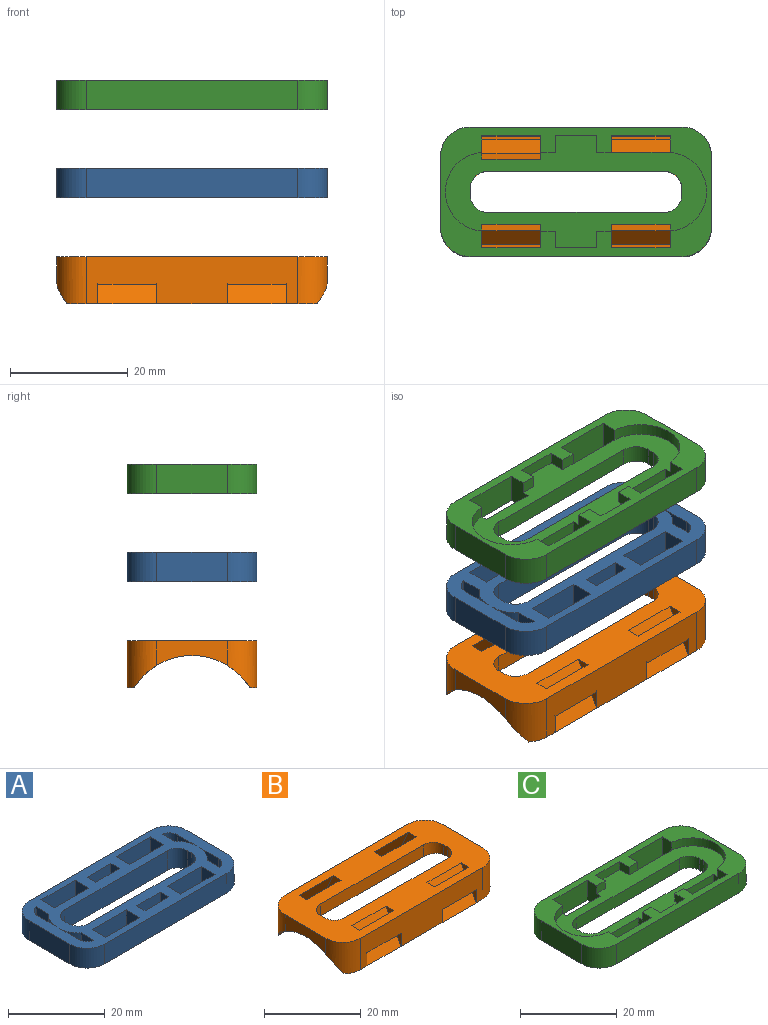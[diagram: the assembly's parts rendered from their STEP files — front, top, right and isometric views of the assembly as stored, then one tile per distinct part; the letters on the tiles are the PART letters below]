
ASSEMBLY  parts=3 mates=2
PART A: 58 faces, bbox 46x22x5 mm
  f0: plane 46x22mm, normal (0,0,1), area 516.2mm2, adj f2,f3,f4,f5,f6,f7,f8,f9
  f1: plane 46x22mm, normal (0,0,-1), area 516.2mm2, adj f2,f3,f4,f5,f6,f7,f8,f9
  f2: plane 36x5mm, normal (0,-1,0), area 180mm2, adj f0,f1,f26,f29
  f3: plane 12x5mm, normal (1,0,0), area 60mm2, adj f0,f1,f26,f27
  f4: plane 36x5mm, normal (0,1,0), area 180mm2, adj f0,f1,f27,f28
  f5: plane 5x1mm, normal (-1,0,0), area 5mm2, adj f0,f1,f30,f33
  f6: plane 30x5mm, normal (0,1,0), area 150mm2, adj f0,f1,f30,f31
  f7: plane 5x1mm, normal (1,0,0), area 5mm2, adj f0,f1,f31,f32
  f8: plane 30x5mm, normal (0,-1,0), area 150mm2, adj f0,f1,f32,f33
  f9: plane 12x5mm, normal (-1,0,0), area 60mm2, adj f0,f1,f28,f29
  f10: plane 10x5mm, normal (0,-1,0), area 50mm2, adj f0,f1,f11,f13
  f11: plane 5x4mm, normal (1,0,0), area 20mm2, adj f0,f1,f10,f12
  f12: plane 10x5mm, normal (0,1,0), area 50mm2, adj f0,f1,f11,f13
  f13: plane 5x4mm, normal (-1,0,0), area 20mm2, adj f0,f1,f10,f12
  f14: plane 10x5mm, normal (0,1,0), area 50mm2, adj f0,f1,f15,f17
  f15: plane 5x4mm, normal (-1,0,0), area 20mm2, adj f0,f1,f14,f16
  f16: plane 10x5mm, normal (0,-1,0), area 50mm2, adj f0,f1,f15,f17
  f17: plane 5x4mm, normal (1,0,0), area 20mm2, adj f0,f1,f14,f16
  f18: plane 5x4mm, normal (-1,0,0), area 20mm2, adj f0,f1,f19,f21
  f19: plane 10x5mm, normal (0,-1,0), area 50mm2, adj f0,f1,f18,f20
  f20: plane 5x4mm, normal (1,0,0), area 20mm2, adj f0,f1,f19,f21
  f21: plane 10x5mm, normal (0,1,0), area 50mm2, adj f0,f1,f18,f20
  f22: plane 5x4mm, normal (-1,0,0), area 20mm2, adj f0,f1,f23,f25
  f23: plane 10x5mm, normal (0,-1,0), area 50mm2, adj f0,f1,f22,f24
  f24: plane 5x4mm, normal (1,0,0), area 20mm2, adj f0,f1,f23,f25
  f25: plane 10x5mm, normal (0,1,0), area 50mm2, adj f0,f1,f22,f24
  f26: cylinder r=5mm len=5mm, axis (0,0,1), area 39.3mm2, adj f0,f1,f2,f3
  f27: cylinder r=5mm len=5mm, axis (0,0,-1), area 39.3mm2, adj f0,f1,f3,f4
  f28: cylinder r=5mm len=5mm, axis (0,0,1), area 39.3mm2, adj f0,f1,f4,f9
  f29: cylinder r=5mm len=5mm, axis (0,0,-1), area 39.3mm2, adj f0,f1,f2,f9
  f30: cylinder r=3mm len=5mm, axis (0,0,-1), area 23.6mm2, adj f0,f1,f5,f6
  f31: cylinder r=3mm len=5mm, axis (0,0,1), area 23.6mm2, adj f0,f1,f6,f7
  f32: cylinder r=3mm len=5mm, axis (0,0,-1), area 23.6mm2, adj f0,f1,f7,f8
  f33: cylinder r=3mm len=5mm, axis (0,0,1), area 23.6mm2, adj f0,f1,f5,f8
  f34: plane 5x2.5mm, normal (1,0,0), area 12.5mm2, adj f0,f1,f36,f37
  f35: plane 5x2.5mm, normal (-1,0,0), area 12.5mm2, adj f0,f1,f36,f37
  f36: plane 7x5mm, normal (0,-1,0), area 35mm2, adj f0,f1,f34,f35
  f37: plane 7x5mm, normal (0,1,0), area 35mm2, adj f0,f1,f34,f35
  f38: cylinder r=5.5mm len=5mm, axis (0,0,-1), area 24.2mm2, adj f0,f1,f40,f41
  f39: cylinder r=2.5mm len=5mm, axis (0,0,1), area 17.1mm2, adj f0,f1,f40,f41
  f40: plane 5x3.71mm, normal (1,0,0), area 18.5mm2, adj f0,f1,f38,f39
  f41: plane 5.5x5mm, normal (-1,0,0), area 27.5mm2, adj f0,f1,f38,f39
  f42: cylinder r=5.5mm len=5mm, axis (0,0,1), area 24.2mm2, adj f0,f1,f44,f45
  f43: cylinder r=2.5mm len=5mm, axis (0,0,-1), area 17.1mm2, adj f0,f1,f44,f45
  f44: plane 5x3.71mm, normal (-1,0,0), area 18.5mm2, adj f0,f1,f42,f43
  f45: plane 5.5x5mm, normal (1,0,0), area 27.5mm2, adj f0,f1,f42,f43
  f46: cylinder r=5.5mm len=5mm, axis (0,0,1), area 24.2mm2, adj f0,f1,f48,f49
  f47: cylinder r=2.5mm len=5mm, axis (0,0,-1), area 17.1mm2, adj f0,f1,f48,f49
  f48: plane 5x3.71mm, normal (1,0,0), area 18.5mm2, adj f0,f1,f46,f47
  f49: plane 5.5x5mm, normal (-1,0,0), area 27.5mm2, adj f0,f1,f46,f47
  f50: plane 7x5mm, normal (0,-1,0), area 35mm2, adj f0,f1,f52,f53
  f51: plane 7x5mm, normal (0,1,0), area 35mm2, adj f0,f1,f52,f53
  f52: plane 5x2.5mm, normal (1,0,0), area 12.5mm2, adj f0,f1,f50,f51
  f53: plane 5x2.5mm, normal (-1,0,0), area 12.5mm2, adj f0,f1,f50,f51
  f54: cylinder r=5.5mm len=5mm, axis (0,0,-1), area 24.2mm2, adj f0,f1,f56,f57
  f55: cylinder r=2.5mm len=5mm, axis (0,0,1), area 17.1mm2, adj f0,f1,f56,f57
  f56: plane 5x3.71mm, normal (-1,0,0), area 18.5mm2, adj f0,f1,f54,f55
  f57: plane 5.5x5mm, normal (1,0,0), area 27.5mm2, adj f0,f1,f54,f55
PART B: 36 faces, bbox 46x22x8 mm
  f0: plane 42.47x1.19mm, normal (0,0,-1), area 48.1mm2, adj f4,f13,f14,f15,f23,f27
  f1: plane 12x4.19mm, normal (1,0,0), area 36.5mm2, adj f10,f11,f14,f15
  f2: plane 36x8mm, normal (0,1,0), area 221.3mm2, adj f9,f10,f11,f12,f28,f29,f30,f32
  f3: plane 12x4.19mm, normal (-1,0,0), area 36.5mm2, adj f10,f12,f13,f15
  f4: plane 36x8mm, normal (0,-1,0), area 221.3mm2, adj f0,f10,f13,f14,f20,f21,f22,f24
  f5: plane 2.51x1mm, normal (-1,0,0), area 2.5mm2, adj f10,f15,f16,f19
  f6: plane 30x3.05mm, normal (0,1,0), area 91.4mm2, adj f10,f15,f16,f17
  f7: plane 2.51x1mm, normal (1,0,0), area 2.5mm2, adj f10,f15,f17,f18
  f8: plane 30x3.05mm, normal (0,-1,0), area 91.4mm2, adj f10,f15,f18,f19
  f9: plane 42.47x1.19mm, normal (0,0,-1), area 48.1mm2, adj f2,f11,f12,f15,f31,f35
  f10: plane 46x22mm, normal (0,0,1), area 654.3mm2, adj f1,f2,f3,f4,f5,f6,f7,f8
  f11: cylinder r=5mm len=8mm, axis (0,0,-1), area 53.8mm2, adj f1,f2,f9,f10,f15
  f12: cylinder r=5mm len=8mm, axis (0,0,1), area 53.8mm2, adj f2,f3,f9,f10,f15
  f13: cylinder r=5mm len=8mm, axis (0,0,-1), area 53.8mm2, adj f0,f3,f4,f10,f15
  f14: cylinder r=5mm len=8mm, axis (0,0,1), area 53.8mm2, adj f0,f1,f4,f10,f15
  f15: cylinder r=11.5mm len=46mm, axis (-1,0,0), area 819.8mm2, adj f0,f1,f3,f5,f6,f7,f8,f9
  f16: cylinder r=3mm len=3.05mm, axis (0,0,-1), area 13.2mm2, adj f5,f6,f10,f15
  f17: cylinder r=3mm len=3.05mm, axis (0,0,1), area 13.2mm2, adj f6,f7,f10,f15
  f18: cylinder r=3mm len=3.05mm, axis (0,0,-1), area 13.2mm2, adj f7,f8,f10,f15
  f19: cylinder r=3mm len=3.05mm, axis (0,0,1), area 13.2mm2, adj f5,f8,f10,f15
  f20: plane 8x4.4mm, normal (1,0,0), area 12.7mm2, adj f4,f10,f21,f23
  f21: plane 10x4.67mm, normal (0,0.91,-0.41), area 51.2mm2, adj f4,f10,f20,f22
  f22: plane 8x4.4mm, normal (-1,0,0), area 12.7mm2, adj f4,f10,f21,f23
  f23: plane 10x8mm, normal (0,-0.88,0.48), area 91.3mm2, adj f0,f10,f20,f22
  f24: plane 8x4.4mm, normal (-1,0,0), area 12.7mm2, adj f4,f10,f25,f27
  f25: plane 10x4.67mm, normal (0,0.91,-0.41), area 51.2mm2, adj f4,f10,f24,f26
  f26: plane 8x4.4mm, normal (1,0,0), area 12.7mm2, adj f4,f10,f25,f27
  f27: plane 10x8mm, normal (0,-0.88,0.48), area 91.3mm2, adj f0,f10,f24,f26
  f28: plane 8x4.4mm, normal (-1,0,0), area 12.7mm2, adj f2,f10,f29,f31
  f29: plane 10x4.67mm, normal (0,-0.91,-0.41), area 51.2mm2, adj f2,f10,f28,f30
  f30: plane 8x4.4mm, normal (1,0,0), area 12.7mm2, adj f2,f10,f29,f31
  f31: plane 10x8mm, normal (0,0.88,0.48), area 91.3mm2, adj f9,f10,f28,f30
  f32: plane 10x4.67mm, normal (0,-0.91,-0.41), area 51.2mm2, adj f2,f10,f33,f34
  f33: plane 8x4.4mm, normal (-1,0,0), area 12.7mm2, adj f2,f10,f32,f35
  f34: plane 8x4.4mm, normal (1,0,0), area 12.7mm2, adj f2,f10,f32,f35
  f35: plane 10x8mm, normal (0,0.88,0.48), area 91.3mm2, adj f9,f10,f33,f34
PART C: 48 faces, bbox 46x22x5 mm
  f0: plane 46x22mm, normal (0,0,1), area 282.9mm2, adj f6,f9,f10,f13,f14,f15,f16,f17
  f1: plane 3x1mm, normal (-1,0,0), area 3mm2, adj f12,f31,f44,f47
  f2: plane 30x3mm, normal (0,1,0), area 90mm2, adj f12,f31,f44,f45
  f3: plane 3x1mm, normal (1,0,0), area 3mm2, adj f12,f31,f45,f46
  f4: plane 30x3mm, normal (0,-1,0), area 90mm2, adj f12,f31,f46,f47
  f5: plane 10x3mm, normal (0,1,0), area 30mm2, adj f6,f12,f18,f31
  f6: plane 5x4mm, normal (-1,0,0), area 17.6mm2, adj f0,f5,f12,f17,f27,f31
  f7: plane 9.5x3mm, normal (0,1,0), area 28.5mm2, adj f12,f19,f20,f31
  f8: plane 10x3mm, normal (0,-1,0), area 30mm2, adj f9,f10,f12,f31
  f9: plane 5x4mm, normal (1,0,0), area 17.6mm2, adj f0,f8,f12,f23,f29,f31
  f10: plane 5x4mm, normal (-1,0,0), area 17.6mm2, adj f0,f8,f12,f23,f31,f36
  f11: plane 10x3mm, normal (0,-1,0), area 30mm2, adj f12,f24,f25,f31
  f12: plane 46x22mm, normal (0,0,-1), area 598.3mm2, adj f1,f2,f3,f4,f5,f6,f7,f8
  f13: plane 36x5mm, normal (0,-1,0), area 180mm2, adj f0,f12,f40,f43
  f14: plane 12x5mm, normal (1,0,0), area 60mm2, adj f0,f12,f40,f41
  f15: plane 36x5mm, normal (0,1,0), area 180mm2, adj f0,f12,f41,f42
  f16: plane 12x5mm, normal (-1,0,0), area 60mm2, adj f0,f12,f42,f43
  f17: plane 10x5mm, normal (0,-1,0), area 50mm2, adj f0,f6,f12,f18
  f18: plane 5x4mm, normal (1,0,0), area 17.6mm2, adj f0,f5,f12,f17,f30,f31
  f19: plane 5x2.8mm, normal (1,0,0), area 14mm2, adj f0,f7,f12,f22,f28
  f20: cylinder r=6.7mm len=3mm, axis (0,0,1), area 1.5mm2, adj f7,f12,f21,f31
  f21: plane 5x2.82mm, normal (-1,0,0), area 14.1mm2, adj f0,f12,f20,f22,f36
  f22: plane 10x5mm, normal (0,-1,0), area 50mm2, adj f0,f12,f19,f21
  f23: plane 10x5mm, normal (0,1,0), area 50mm2, adj f0,f9,f10,f12
  f24: plane 5x4mm, normal (-1,0,0), area 17.6mm2, adj f0,f11,f12,f26,f31,f32
  f25: plane 5x4mm, normal (1,0,0), area 17.6mm2, adj f0,f11,f12,f26,f30,f31
  f26: plane 10x5mm, normal (0,1,0), area 50mm2, adj f0,f12,f24,f25
  f27: plane 2.5x2mm, normal (0,-1,0), area 5mm2, adj f0,f6,f31,f39
  f28: plane 2.5x2mm, normal (0,-1,0), area 5mm2, adj f0,f19,f31,f37
  f29: plane 2.5x2mm, normal (0,1,0), area 5mm2, adj f0,f9,f31,f35
  f30: cylinder r=6.7mm len=13.36mm, axis (0,0,1), area 40.1mm2, adj f0,f18,f25,f31
  f31: plane 44.4x19mm, normal (0,0,1), area 315.4mm2, adj f1,f2,f3,f4,f5,f6,f7,f8
  f32: plane 2.5x2mm, normal (0,1,0), area 5mm2, adj f0,f24,f31,f33
  f33: plane 2.8x2mm, normal (1,0,0), area 5.6mm2, adj f0,f31,f32,f34
  f34: plane 7x2mm, normal (0,1,0), area 14mm2, adj f0,f31,f33,f35
  f35: plane 2.8x2mm, normal (-1,0,0), area 5.6mm2, adj f0,f29,f31,f34
  f36: cylinder r=6.7mm len=13.36mm, axis (0,0,1), area 40.1mm2, adj f0,f10,f21,f31
  f37: plane 2.8x2mm, normal (-1,0,0), area 5.6mm2, adj f0,f28,f31,f38
  f38: plane 7x2mm, normal (0,-1,0), area 14mm2, adj f0,f31,f37,f39
  f39: plane 2.8x2mm, normal (1,0,0), area 5.6mm2, adj f0,f27,f31,f38
  f40: cylinder r=5mm len=5mm, axis (0,0,1), area 39.3mm2, adj f0,f12,f13,f14
  f41: cylinder r=5mm len=5mm, axis (0,0,-1), area 39.3mm2, adj f0,f12,f14,f15
  f42: cylinder r=5mm len=5mm, axis (0,0,1), area 39.3mm2, adj f0,f12,f15,f16
  f43: cylinder r=5mm len=5mm, axis (0,0,-1), area 39.3mm2, adj f0,f12,f13,f16
  f44: cylinder r=3mm len=3mm, axis (0,0,-1), area 14.1mm2, adj f1,f2,f12,f31
  f45: cylinder r=3mm len=3mm, axis (0,0,1), area 14.1mm2, adj f2,f3,f12,f31
  f46: cylinder r=3mm len=3mm, axis (0,0,-1), area 14.1mm2, adj f3,f4,f12,f31
  f47: cylinder r=3mm len=3mm, axis (0,0,1), area 14.1mm2, adj f1,f4,f12,f31
PLACE A t=(-24.63,-17.61,12.91)mm
PLACE B t=(-24.63,-17.61,-5.09)mm fixed
PLACE C rot(axis=(0,0,1),0deg) t=(-24.63,-17.61,27.91)mm
MATE parallel A.f0 <-> C.f12  axis (0,0,1) through (-42.63,-28.61,17.91)mm
MATE parallel B.f10 <-> A.f1  axis (0,0,1) through (-24.63,-17.61,2.91)mm
